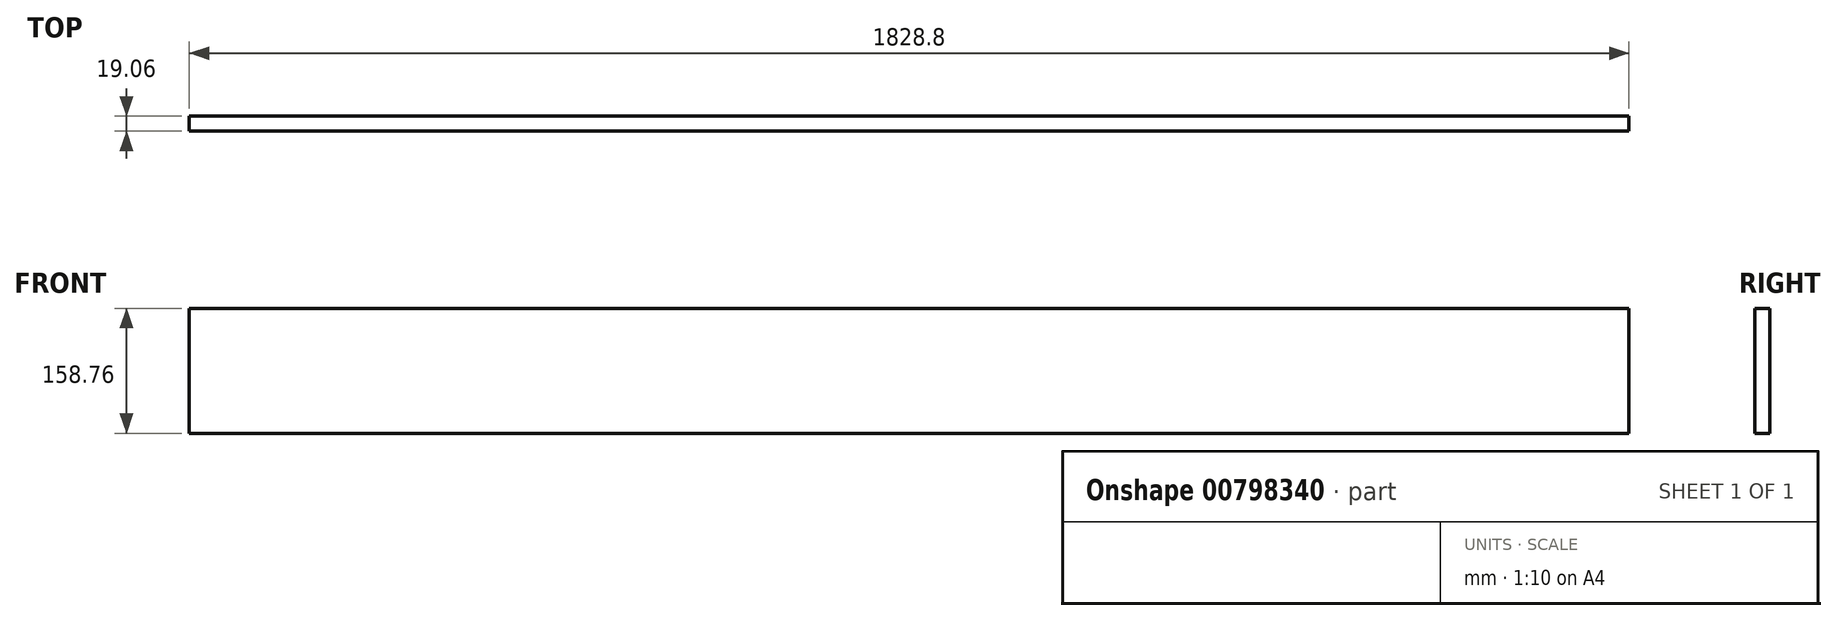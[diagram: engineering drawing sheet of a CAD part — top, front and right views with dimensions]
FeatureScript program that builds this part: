
annotation { "Feature Type Name" : "Feature", "Feature Type Description" : "" }
export const myFeature = defineFeature(function(context is Context, id is Id, definition is map)
    precondition{}
    {
        {
            var Q0;
            Q0=qCreatedBy(makeId("Right.planeOp"),FACE);
            var sketch = newSketch(context, id + "F0", { "sketchPlane" : qUnion([Q0])});
            skLineSegment(sketch, "E0.bottom", {"start": v(9.53, 79.38) * mm, "end": v(-9.52, 79.38) * mm});
            skLineSegment(sketch, "E0.top", {"start": v(9.53, -79.38) * mm, "end": v(-9.53, -79.38) * mm});
            skLineSegment(sketch, "E0.left", {"start": v(9.53, 79.38) * mm, "end": v(9.53, -79.38) * mm});
            skLineSegment(sketch, "E0.right", {"start": v(-9.52, 79.38) * mm, "end": v(-9.53, -79.38) * mm});
            skPoint(sketch, "E0.middle", {"position": v(0, 0) * mm});
            skSolve(sketch);
        }
        {
            var Q0;
            Q0 = qSketchRegion(id + "F0", true);
            extrude(context, id + "F1", {"entities" : qUnion([Q0]), "depth" : 1828.8 * mm, "offsetDistance" : 25.4 * mm});
        }
    });
